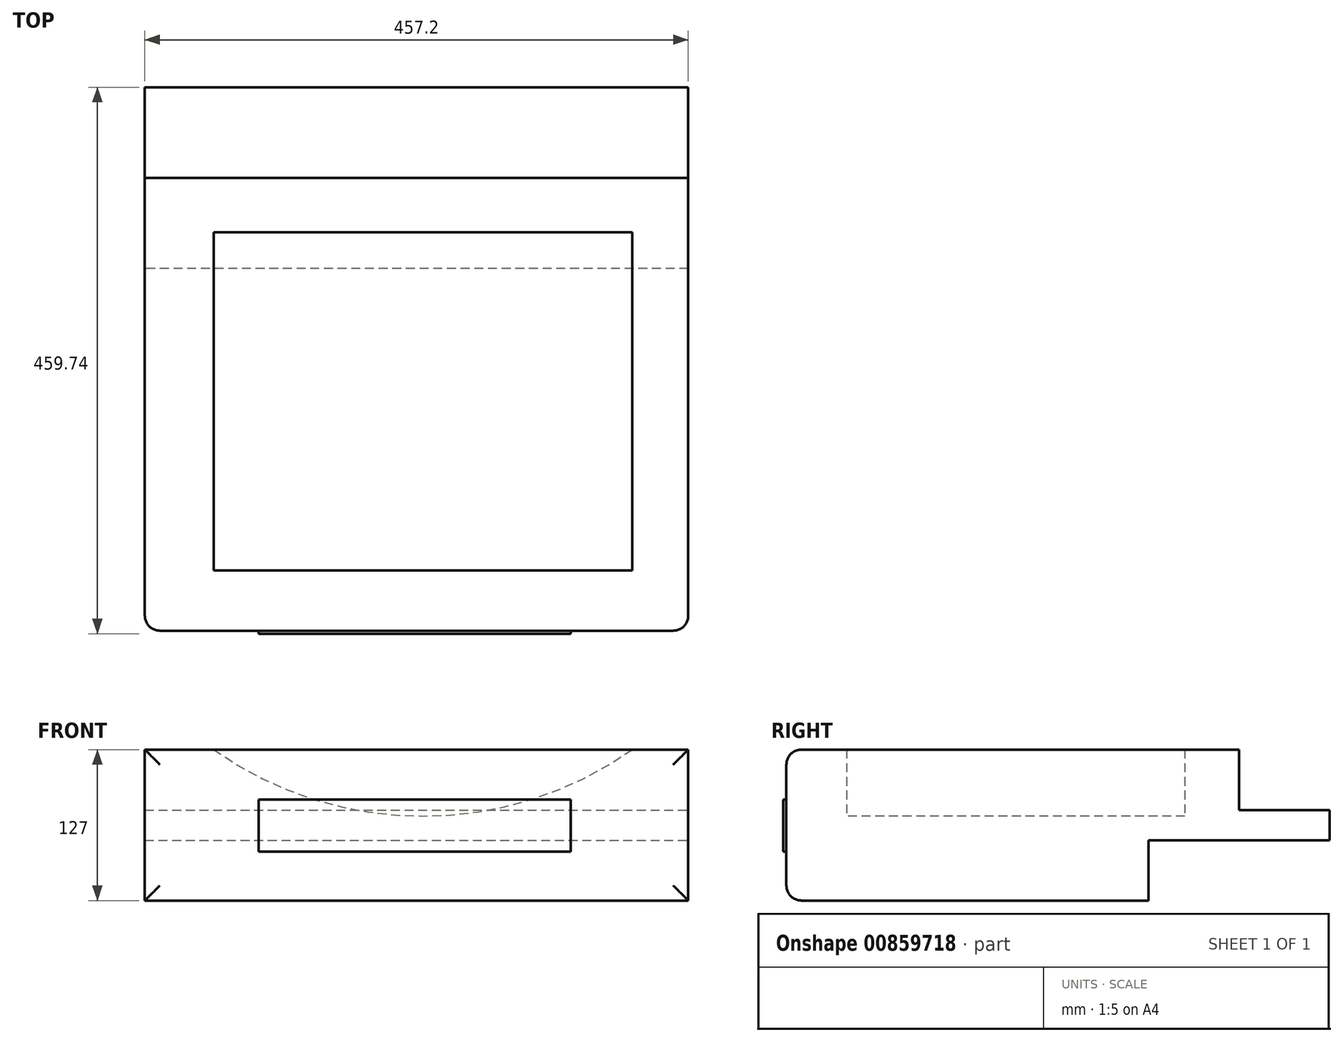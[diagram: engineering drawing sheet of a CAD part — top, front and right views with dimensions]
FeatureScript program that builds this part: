
annotation { "Feature Type Name" : "Feature", "Feature Type Description" : "" }
export const myFeature = defineFeature(function(context is Context, id is Id, definition is map)
    precondition{}
    {
        {
            var Q0;
            Q0=qCreatedBy(makeId("Front.planeOp"),FACE);
            var sketch = newSketch(context, id + "F0", { "sketchPlane" : qUnion([Q0])});
            skLineSegment(sketch, "E0.bottom", {"start": v(-233.9, 56.72) * mm, "end": v(223.3, 56.72) * mm});
            skLineSegment(sketch, "E0.top", {"start": v(-233.9, -70.28) * mm, "end": v(223.3, -70.28) * mm});
            skLineSegment(sketch, "E0.left", {"start": v(-233.9, 56.72) * mm, "end": v(-233.9, -70.28) * mm});
            skLineSegment(sketch, "E0.right", {"start": v(223.3, 56.72) * mm, "end": v(223.3, -70.28) * mm});
            skSolve(sketch);
        }
        {
            var Q0;
            Q0 = qSketchRegion(id + "F0", true);
            extrude(context, id + "F1", {"entities" : qUnion([Q0]), "depth" : 457.2 * mm, "offsetDistance" : 25.4 * mm});
        }
        {
            var Q0;
            Q0=makeQuery(id+"F1.opExtrude","CAP_FACE",FACE,{"disambiguationData":[OSD([sQuery(id+"F0.wireOp",EDGE,"E0.bottom"),sQuery(id+"F0.wireOp",EDGE,"E0.top"),sQuery(id+"F0.wireOp",EDGE,"E0.left"),sQuery(id+"F0.wireOp",EDGE,"E0.right")])],"isStart":false});
            fillet(context, id + "F2", {"entities" : qUnion([Q0]), "radius" : 12.7 * mm, "tangentPropagation" : true, "allowEdgeOverflow" : false});
        }
        {
            var Q0;
            Q0=makeQuery(id+"F1.opExtrude","SWEPT_FACE",FACE,{"disambiguationData":[OSD([sQuery(id+"F0.wireOp",EDGE,"E0.bottom")])]});
            var sketch = newSketch(context, id + "F3", { "sketchPlane" : qUnion([Q0])});
            skLineSegment(sketch, "E1.bottom", {"start": v(-233.9, 0) * mm, "end": v(223.3, 0) * mm});
            skLineSegment(sketch, "E1.top", {"start": v(-233.9, -76.2) * mm, "end": v(223.3, -76.2) * mm});
            skLineSegment(sketch, "E1.left", {"start": v(-233.9, 0) * mm, "end": v(-233.9, -76.2) * mm});
            skLineSegment(sketch, "E1.right", {"start": v(223.3, 0) * mm, "end": v(223.3, -76.2) * mm});
            skSolve(sketch);
        }
        {
            var Q0;
            Q0=makeQuery(id+"F3.imprint","IMPRINT",FACE,{"disambiguationData":[TD([[makeQuery(id+"F3.imprint","IMPRINT",EDGE,{"derivedFrom":sQuery(id+"F3.wireOp",EDGE,"E1.bottom")}),-1.0]])]});
            extrude(context, id + "F4", {"entities" : qUnion([Q0]), "operationType" : NewBodyOperationType.REMOVE, "oppositeDirection" : true, "depth" : 50.8 * mm, "offsetDistance" : 25.4 * mm});
        }
        {
            var Q0;
            Q0=makeQuery(id+"F1.opExtrude","CAP_FACE",FACE,{"disambiguationData":[OSD([sQuery(id+"F0.wireOp",EDGE,"E0.bottom"),sQuery(id+"F0.wireOp",EDGE,"E0.top"),sQuery(id+"F0.wireOp",EDGE,"E0.left"),sQuery(id+"F0.wireOp",EDGE,"E0.right")])],"isStart":false});
            var sketch = newSketch(context, id + "F5", { "sketchPlane" : qUnion([Q0])});
            skCircle(sketch, "E2", {"center": v(0, 305.54) * mm, "radius": 304.8 * mm});
            skSolve(sketch);
        }
        {
            var Q0;
            {var subQ0=sQuery(id+"F5.wireOp",EDGE,"E2");var subQ1=sQuery(id+"F0.wireOp",EDGE,"E0.bottom");var subQ2=makeQuery(id+"F2.opFillet","BLEND_EDGE",EDGE,{"blendedFrom":[makeQuery(id+"F1.opExtrude","CAP_EDGE",EDGE,{"disambiguationData":[OSD([subQ1])],"isStart":false}),makeQuery(id+"F1.opExtrude","CAP_FACE",FACE,{"disambiguationData":[OSD([subQ1,sQuery(id+"F0.wireOp",EDGE,"E0.top"),sQuery(id+"F0.wireOp",EDGE,"E0.left"),sQuery(id+"F0.wireOp",EDGE,"E0.right")])],"isStart":false})],"blendedInto":[makeQuery(id+"F1.opExtrude","CAP_FACE",FACE,{"disambiguationData":[OSD([subQ1,sQuery(id+"F0.wireOp",EDGE,"E0.top"),sQuery(id+"F0.wireOp",EDGE,"E0.left"),sQuery(id+"F0.wireOp",EDGE,"E0.right")])],"isStart":false})]});var subQ3=makeQuery(id+"F5.imprint","INTERSECT",VERTEX,{"disambiguationData":[OD(0.0)],"derivedFrom":[subQ2,subQ0]});Q0=makeQuery(id+"F5.imprint","IMPRINT",FACE,{"disambiguationData":[TD([[makeQuery(id+"F5.imprint","IMPRINT",EDGE,{"disambiguationData":[TD([[subQ3,-1.0]])],"derivedFrom":subQ0}),1.0]])]});}
            var Q1;
            {var subQ0=sQuery(id+"F5.wireOp",EDGE,"E2");var subQ1=sQuery(id+"F0.wireOp",EDGE,"E0.bottom");var subQ2=makeQuery(id+"F2.opFillet","BLEND_EDGE",EDGE,{"blendedFrom":[makeQuery(id+"F1.opExtrude","CAP_EDGE",EDGE,{"disambiguationData":[OSD([subQ1])],"isStart":false}),makeQuery(id+"F1.opExtrude","CAP_FACE",FACE,{"disambiguationData":[OSD([subQ1,sQuery(id+"F0.wireOp",EDGE,"E0.top"),sQuery(id+"F0.wireOp",EDGE,"E0.left"),sQuery(id+"F0.wireOp",EDGE,"E0.right")])],"isStart":false})],"blendedInto":[makeQuery(id+"F1.opExtrude","CAP_FACE",FACE,{"disambiguationData":[OSD([subQ1,sQuery(id+"F0.wireOp",EDGE,"E0.top"),sQuery(id+"F0.wireOp",EDGE,"E0.left"),sQuery(id+"F0.wireOp",EDGE,"E0.right")])],"isStart":false})]});var subQ3=makeQuery(id+"F5.imprint","INTERSECT",VERTEX,{"disambiguationData":[OD(0.0)],"derivedFrom":[subQ2,subQ0]});Q1=makeQuery(id+"F5.imprint","IMPRINT",FACE,{"disambiguationData":[TD([[makeQuery(id+"F5.imprint","IMPRINT",EDGE,{"disambiguationData":[TD([[subQ3,1.0]])],"derivedFrom":subQ0}),1.0]])]});}
            extrude(context, id + "F6", {"entities" : qUnion([Q0, Q1]), "operationType" : NewBodyOperationType.REMOVE, "oppositeDirection" : true, "depth" : 335.28 * mm, "offsetDistance" : 25.4 * mm, "hasSecondDirection" : true, "secondDirectionOppositeDirection" : true, "secondDirectionDepth" : 50.8 * mm});
        }
        {
            var Q0;
            Q0=makeQuery(id+"F1.opExtrude","CAP_FACE",FACE,{"disambiguationData":[OSD([sQuery(id+"F0.wireOp",EDGE,"E0.bottom"),sQuery(id+"F0.wireOp",EDGE,"E0.top"),sQuery(id+"F0.wireOp",EDGE,"E0.left"),sQuery(id+"F0.wireOp",EDGE,"E0.right")])],"isStart":false});
            var sketch = newSketch(context, id + "F7", { "sketchPlane" : qUnion([Q0])});
            skLineSegment(sketch, "E3.bottom", {"start": v(-138.26, 14.62) * mm, "end": v(124.27, 14.62) * mm});
            skLineSegment(sketch, "E3.top", {"start": v(-138.26, -29.15) * mm, "end": v(124.27, -29.15) * mm});
            skLineSegment(sketch, "E3.left", {"start": v(-138.26, 14.62) * mm, "end": v(-138.26, -29.15) * mm});
            skLineSegment(sketch, "E3.right", {"start": v(124.27, 14.62) * mm, "end": v(124.27, -29.15) * mm});
            skSolve(sketch);
        }
        {
            var Q0;
            Q0=makeQuery(id+"F7.imprint","IMPRINT",FACE,{"disambiguationData":[TD([[makeQuery(id+"F7.imprint","IMPRINT",EDGE,{"derivedFrom":sQuery(id+"F7.wireOp",EDGE,"E3.bottom")}),-1.0]])]});
            var Q1;
            Q1=sQuery(id+"F7.wireOp",EDGE,"E3.left");
            var Q2;
            Q2=sQuery(id+"F7.wireOp",EDGE,"E3.bottom");
            var Q3;
            Q3=sQuery(id+"F7.wireOp",EDGE,"E3.right");
            var Q4;
            Q4=sQuery(id+"F7.wireOp",EDGE,"E3.top");
            extrude(context, id + "F8", {"entities" : qUnion([Q0]), "surfaceEntities" : qUnion([Q1, Q2, Q3, Q4]), "depth" : 2.54 * mm, "offsetDistance" : 25.4 * mm});
        }
        {
            var Q0;
            Q0=makeQuery(id+"F1.opExtrude","SWEPT_FACE",FACE,{"disambiguationData":[OSD([sQuery(id+"F0.wireOp",EDGE,"E0.top")])]});
            var sketch = newSketch(context, id + "F9", { "sketchPlane" : qUnion([Q0])});
            skLineSegment(sketch, "E4.bottom", {"start": v(223.3, 0) * mm, "end": v(-233.9, 0) * mm});
            skLineSegment(sketch, "E4.top", {"start": v(223.3, 152.4) * mm, "end": v(-233.9, 152.4) * mm});
            skLineSegment(sketch, "E4.left", {"start": v(223.3, 0) * mm, "end": v(223.3, 152.4) * mm});
            skLineSegment(sketch, "E4.right", {"start": v(-233.9, 0) * mm, "end": v(-233.9, 152.4) * mm});
            skSolve(sketch);
        }
        {
            var Q0;
            Q0=makeQuery(id+"F9.imprint","IMPRINT",FACE,{"disambiguationData":[TD([[makeQuery(id+"F9.imprint","IMPRINT",EDGE,{"derivedFrom":sQuery(id+"F9.wireOp",EDGE,"E4.bottom")}),1.0]])]});
            extrude(context, id + "F10", {"entities" : qUnion([Q0]), "operationType" : NewBodyOperationType.REMOVE, "oppositeDirection" : true, "depth" : 50.8 * mm, "offsetDistance" : 25.4 * mm});
        }
    });
